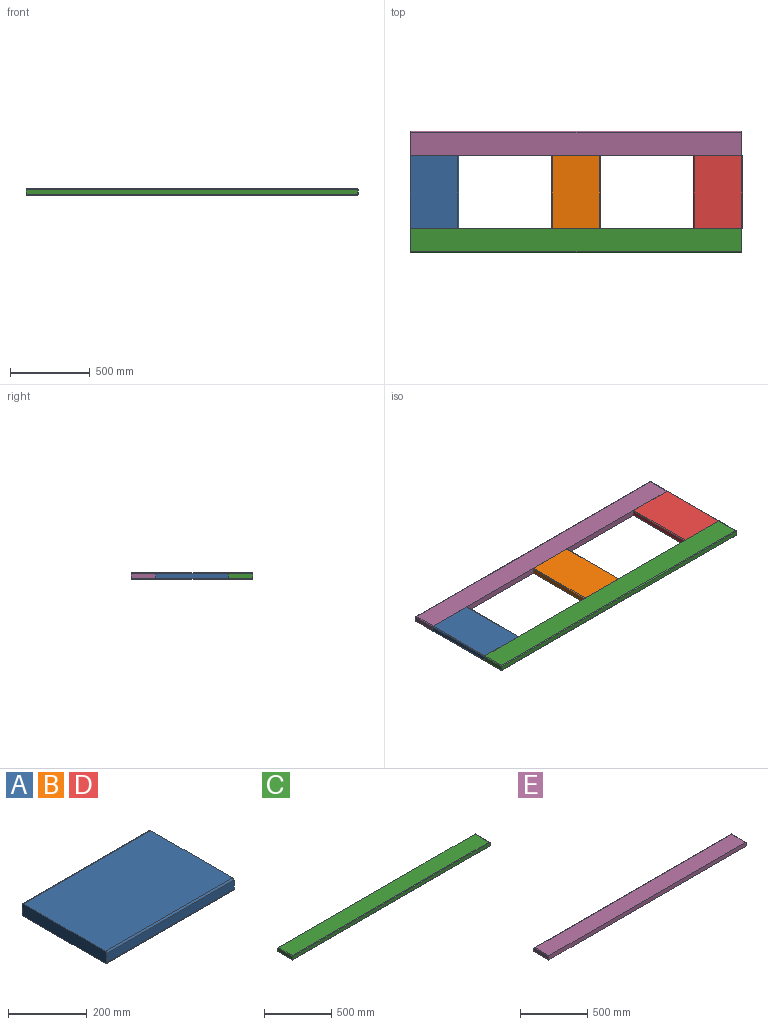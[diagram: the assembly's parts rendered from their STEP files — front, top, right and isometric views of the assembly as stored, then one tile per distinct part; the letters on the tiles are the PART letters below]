
ASSEMBLY  parts=5 mates=4
PART A: 10 faces, bbox 457.2x304.8x38.1 mm
  f0: plane 304.8x38.1mm, normal (-1,0,0), area 11590.7mm2, adj f1,f3,f4,f5,f6,f7,f8,f9
  f1: plane 457.2x27.94mm, normal (0,-1,0), area 12774.2mm2, adj f0,f2,f6,f8
  f2: plane 304.8x38.1mm, normal (1,0,0), area 11590.7mm2, adj f1,f3,f4,f5,f6,f7,f8,f9
  f3: plane 457.2x27.94mm, normal (0,1,0), area 12774.2mm2, adj f0,f2,f7,f9
  f4: plane 457.2x294.64mm, normal (0,0,1), area 134709.4mm2, adj f0,f2,f8,f9
  f5: plane 457.2x294.64mm, normal (0,0,-1), area 134709.4mm2, adj f0,f2,f6,f7
  f6: cylinder r=5.08mm len=457.2mm, axis (1,0,0), area 3648.3mm2, adj f0,f1,f2,f5
  f7: cylinder r=5.08mm len=457.2mm, axis (-1,0,0), area 3648.3mm2, adj f0,f2,f3,f5
  f8: cylinder r=5.08mm len=457.2mm, axis (-1,0,0), area 3648.3mm2, adj f0,f1,f2,f4
  f9: cylinder r=5.08mm len=457.2mm, axis (1,0,0), area 3648.3mm2, adj f0,f2,f3,f4
PART B: same geometry as A
PART C: 12 faces, bbox 2082.8x152.4x38.1 mm
  f0: plane 152.4x27.94mm, normal (-1,0,0), area 4258.1mm2, adj f1,f3,f6,f9
  f1: plane 2082.8x27.94mm, normal (0,-1,0), area 58193.4mm2, adj f0,f2,f7,f10
  f2: plane 152.4x27.94mm, normal (1,0,0), area 4258.1mm2, adj f1,f3,f8,f11
  f3: plane 2082.8x38.1mm, normal (0,1,0), area 79332.5mm2, adj f0,f2,f4,f5,f6,f8,f9,f11
  f4: plane 2072.64x147.32mm, normal (0,0,1), area 305341.3mm2, adj f3,f9,f10,f11
  f5: plane 2072.64x147.32mm, normal (0,0,-1), area 305341.3mm2, adj f3,f6,f7,f8
  f6: cylinder r=5.08mm len=152.4mm, axis (0,-1,0), area 1201.4mm2, adj f0,f3,f5,f7
  f7: cylinder r=5.08mm len=2082.8mm, axis (1,0,0), area 16590.5mm2, adj f1,f5,f6,f8
  f8: cylinder r=5.08mm len=152.4mm, axis (0,1,0), area 1201.4mm2, adj f2,f3,f5,f7
  f9: cylinder r=5.08mm len=152.4mm, axis (0,1,0), area 1201.4mm2, adj f0,f3,f4,f10
  f10: cylinder r=5.08mm len=2082.8mm, axis (-1,0,0), area 16590.5mm2, adj f1,f4,f9,f11
  f11: cylinder r=5.08mm len=152.4mm, axis (0,-1,0), area 1201.4mm2, adj f2,f3,f4,f10
PART D: same geometry as A
PART E: 12 faces, bbox 2082.8x152.4x38.1 mm
  f0: plane 152.4x27.94mm, normal (-1,0,0), area 4258.1mm2, adj f1,f3,f6,f9
  f1: plane 2082.8x38.1mm, normal (0,-1,0), area 79332.5mm2, adj f0,f2,f4,f5,f6,f8,f9,f11
  f2: plane 152.4x27.94mm, normal (1,0,0), area 4258.1mm2, adj f1,f3,f8,f11
  f3: plane 2082.8x27.94mm, normal (0,1,0), area 58193.4mm2, adj f0,f2,f7,f10
  f4: plane 2072.64x147.32mm, normal (0,0,1), area 305341.3mm2, adj f1,f9,f10,f11
  f5: plane 2072.64x147.32mm, normal (0,0,-1), area 305341.3mm2, adj f1,f6,f7,f8
  f6: cylinder r=5.08mm len=152.4mm, axis (0,-1,0), area 1201.4mm2, adj f0,f1,f5,f7
  f7: cylinder r=5.08mm len=2082.8mm, axis (-1,0,0), area 16590.5mm2, adj f3,f5,f6,f8
  f8: cylinder r=5.08mm len=152.4mm, axis (0,1,0), area 1201.4mm2, adj f1,f2,f5,f7
  f9: cylinder r=5.08mm len=152.4mm, axis (0,1,0), area 1201.4mm2, adj f0,f1,f4,f10
  f10: cylinder r=5.08mm len=2082.8mm, axis (1,0,0), area 16590.5mm2, adj f3,f4,f9,f11
  f11: cylinder r=5.08mm len=152.4mm, axis (0,-1,0), area 1201.4mm2, adj f1,f2,f4,f10
PLACE A rot(axis=(0,0,-1),90deg) t=(-923.65,-614.65,134.9)mm
PLACE B rot(axis=(0,0,-1),90deg) t=(-34.65,-614.65,134.9)mm
PLACE C rot(axis=(0,-0.05,1),0deg) t=(-605.19,-779.77,134.9)mm
PLACE D rot(axis=(0,0,-1),90deg) t=(854.35,-614.65,134.9)mm
PLACE E rot(axis=(0.02,-0.08,1),0deg) t=(-605.19,-170.17,134.9)mm
MATE fastened B.f2 <-> C.f3  axis (0,-1,0) through (54.74,-690.38,134.9)mm
MATE fastened C.f3 <-> D.f2  axis (0,1,0) through (1096.14,-690.38,153.95)mm
MATE fastened E.f1 <-> D.f0  axis (0,-1,0) through (1096.14,-233.18,153.95)mm
MATE fastened A.f2 <-> C.f3  axis (0,-1,0) through (-986.66,-690.38,153.95)mm
